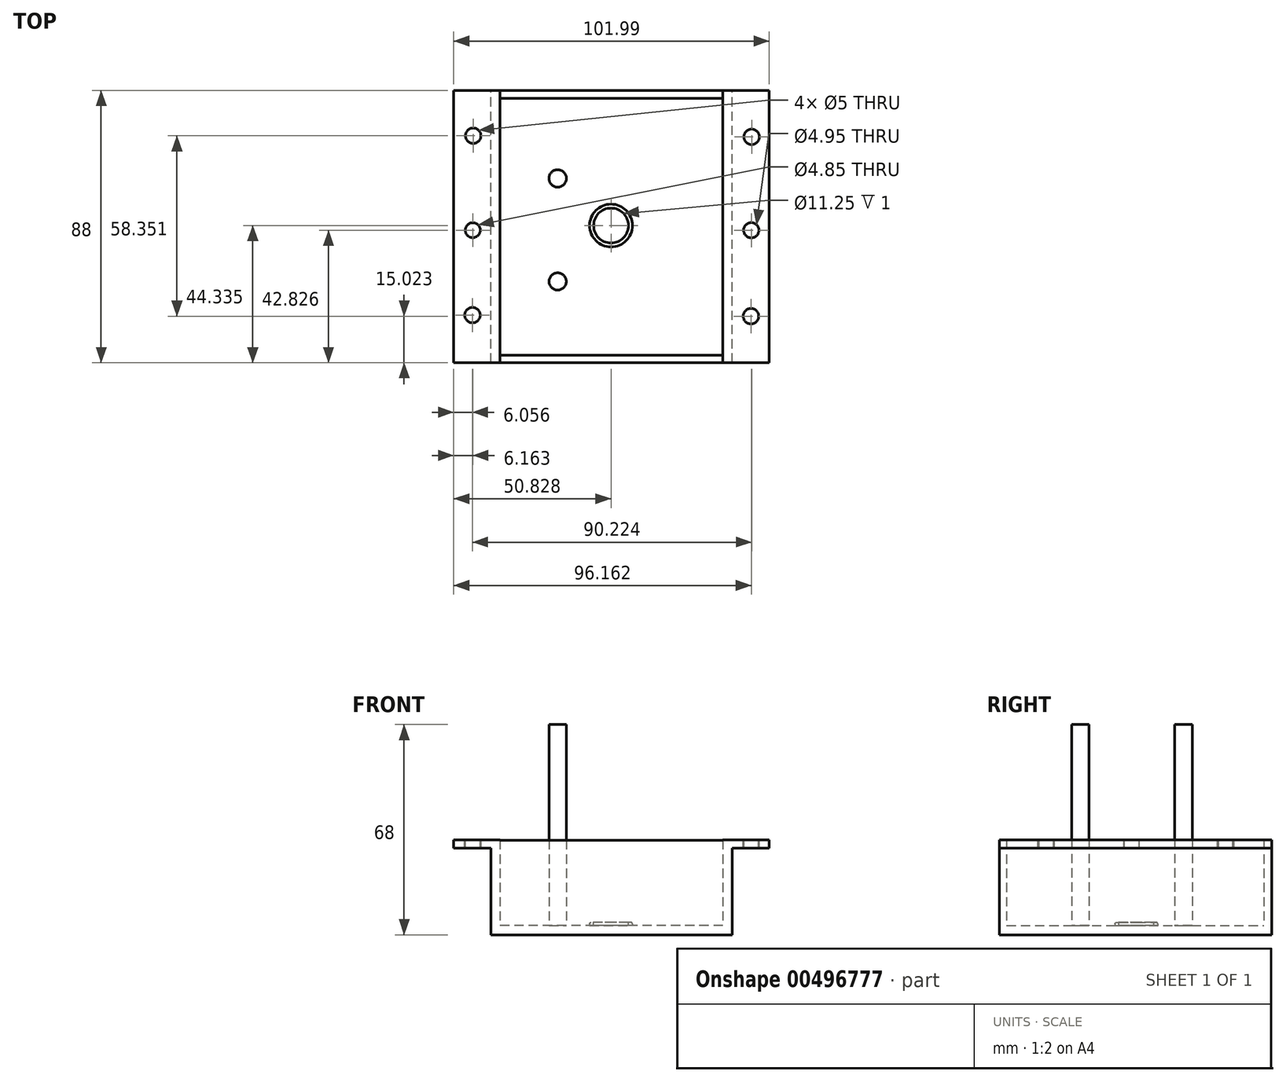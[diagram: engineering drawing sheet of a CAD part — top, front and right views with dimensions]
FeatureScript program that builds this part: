
annotation { "Feature Type Name" : "Feature", "Feature Type Description" : "" }
export const myFeature = defineFeature(function(context is Context, id is Id, definition is map)
    precondition{}
    {
        {
            var Q0;
            Q0=qCreatedBy(makeId("Front.planeOp"),FACE);
            var sketch = newSketch(context, id + "F0", { "sketchPlane" : qUnion([Q0])});
            skLineSegment(sketch, "E0", {"start": v(-2.97, -6.62) * mm, "end": v(-2.97, -9.62) * mm});
            skLineSegment(sketch, "E1", {"start": v(-2.97, -9.62) * mm, "end": v(36.03, -9.62) * mm});
            skLineSegment(sketch, "E2", {"start": v(36.03, -9.62) * mm, "end": v(36.03, 18.38) * mm});
            skLineSegment(sketch, "E3", {"start": v(36.03, 18.38) * mm, "end": v(48.02, 18.38) * mm});
            skLineSegment(sketch, "E4", {"start": v(48.02, 18.38) * mm, "end": v(48.02, 21.12) * mm});
            skLineSegment(sketch, "E5", {"start": v(48.02, 21.12) * mm, "end": v(33.02, 21.12) * mm});
            skLineSegment(sketch, "E6", {"start": v(33.02, 21.12) * mm, "end": v(33.02, -6.62) * mm});
            skLineSegment(sketch, "E7", {"start": v(33.02, -6.62) * mm, "end": v(-2.97, -6.62) * mm});
            skLineSegment(sketch, "E8.MirrorCS", {"start": v(-53.97, 18.38) * mm, "end": v(-53.97, 21.12) * mm});
            skLineSegment(sketch, "E9.MirrorCS", {"start": v(-41.97, -9.62) * mm, "end": v(-41.97, 18.38) * mm});
            skLineSegment(sketch, "E10.MirrorCS", {"start": v(-41.97, 18.38) * mm, "end": v(-53.97, 18.38) * mm});
            skLineSegment(sketch, "E11.MirrorCS", {"start": v(-53.97, 21.12) * mm, "end": v(-38.97, 21.12) * mm});
            skLineSegment(sketch, "E12.MirrorCS", {"start": v(-38.97, 21.12) * mm, "end": v(-38.97, -6.62) * mm});
            skLineSegment(sketch, "E13.MirrorCS", {"start": v(-2.97, -9.62) * mm, "end": v(-41.97, -9.62) * mm});
            skLineSegment(sketch, "E14.MirrorCS", {"start": v(-38.97, -6.62) * mm, "end": v(-2.97, -6.62) * mm});
            skPoint(sketch, "E15.MirrorCS.start.orphan", {"position": v(36.03, 18.38) * mm});
            skSolve(sketch);
        }
        {
            var Q0;
            Q0=qSketchRegion(id+"F0",true);
            extrude(context, id + "F1", {"entities" : qUnion([Q0]), "endBound" : BoundingType.SYMMETRIC, "depth" : 88 * mm});
        }
        {
            var Q0;
            Q0=makeQuery(id+"F1.opExtrude","SWEPT_FACE",FACE,{"disambiguationData":[OSD([sQuery(id+"F0.wireOp",EDGE,"E5")])]});
            var sketch = newSketch(context, id + "F2", { "sketchPlane" : qUnion([Q0])});
            skLineSegment(sketch, "E16", {"start": v(42.02, -44) * mm, "end": v(42.33, 34) * mm, "construction": true});
            skLineSegment(sketch, "E17.0.0", {"start": v(-38.97, 44) * mm, "end": v(-53.97, 44) * mm, "construction": true});
            skLineSegment(sketch, "E17.0.1", {"start": v(-53.97, 44) * mm, "end": v(-53.97, -44) * mm, "construction": true});
            skLineSegment(sketch, "E17.0.2", {"start": v(-53.97, -44) * mm, "end": v(-38.97, -44) * mm, "construction": true});
            skLineSegment(sketch, "E17.0.3", {"start": v(-38.97, -44) * mm, "end": v(-38.97, 44) * mm, "construction": true});
            skLineSegment(sketch, "E18", {"start": v(-47.67, 34) * mm, "end": v(-47.97, -44) * mm, "construction": true});
            skLineSegment(sketch, "E19", {"start": v(-53.97, -28.6) * mm, "end": v(48.02, -29) * mm, "construction": true});
            skLineSegment(sketch, "E20", {"start": v(48.02, 29) * mm, "end": v(-53.97, 29.4) * mm, "construction": true});
            skLineSegment(sketch, "E21", {"start": v(48.02, -29) * mm, "end": v(48.02, -44) * mm, "construction": true});
            skLineSegment(sketch, "E22", {"start": v(48.02, 44) * mm, "end": v(48.02, 29) * mm, "construction": true});
            skCircle(sketch, "E23", {"center": v(42.08, -28.98) * mm, "radius": 2.5 * mm});
            skCircle(sketch, "E24", {"center": v(42.31, 29.02) * mm, "radius": 2.5 * mm});
            skCircle(sketch, "E25", {"center": v(-47.69, 29.37) * mm, "radius": 2.5 * mm});
            skCircle(sketch, "E26", {"center": v(-47.91, -28.63) * mm, "radius": 2.5 * mm});
            skCircle(sketch, "E27", {"center": v(42.2, -1.17) * mm, "radius": 2.47 * mm});
            skCircle(sketch, "E28", {"center": v(-47.8, -1.17) * mm, "radius": 2.43 * mm});
            skSolve(sketch);
        }
        {
            var Q0;
            Q0=qSketchRegion(id+"F2",true);
            extrude(context, id + "F3", {"entities" : qUnion([Q0]), "operationType" : NewBodyOperationType.REMOVE, "endBound" : BoundingType.UP_TO_NEXT, "oppositeDirection" : true, "depth" : 25 * mm});
        }
        {
            var Q0;
            Q0=makeQuery(id+"F1.opExtrude","SWEPT_FACE",FACE,{"disambiguationData":[OSD([sQuery(id+"F0.wireOp",EDGE,"E7"),sQuery(id+"F0.wireOp",EDGE,"E14.MirrorCS")])]});
            var sketch = newSketch(context, id + "F4", { "sketchPlane" : qUnion([Q0])});
            skLineSegment(sketch, "E29.bottom", {"start": v(33.02, 44) * mm, "end": v(-38.97, 44) * mm});
            skLineSegment(sketch, "E29.top", {"start": v(33.02, 41.5) * mm, "end": v(-38.97, 41.5) * mm});
            skLineSegment(sketch, "E29.left", {"start": v(33.02, 44) * mm, "end": v(33.02, 41.5) * mm});
            skLineSegment(sketch, "E29.right", {"start": v(-38.97, 44) * mm, "end": v(-38.97, 41.5) * mm});
            skLineSegment(sketch, "E30.bottom", {"start": v(33.02, -44) * mm, "end": v(-38.97, -44) * mm});
            skLineSegment(sketch, "E30.top", {"start": v(33.02, -41.63) * mm, "end": v(-38.97, -41.63) * mm});
            skLineSegment(sketch, "E30.left", {"start": v(33.02, -44) * mm, "end": v(33.02, -41.63) * mm});
            skLineSegment(sketch, "E30.right", {"start": v(-38.97, -44) * mm, "end": v(-38.97, -41.63) * mm});
            skSolve(sketch);
        }
        {
            var Q0;
            Q0=qSketchRegion(id+"F4",true);
            extrude(context, id + "F5", {"entities" : qUnion([Q0]), "operationType" : NewBodyOperationType.ADD, "depth" : 27.6 * mm});
        }
        {
            var Q0;
            Q0=makeQuery(id+"F1.opExtrude","SWEPT_FACE",FACE,{"disambiguationData":[OSD([sQuery(id+"F0.wireOp",EDGE,"E7"),sQuery(id+"F0.wireOp",EDGE,"E14.MirrorCS")])]});
            var sketch = newSketch(context, id + "F6", { "sketchPlane" : qUnion([Q0])});
            skCircle(sketch, "E31", {"center": v(-3.14, 0.33) * mm, "radius": 6.92 * mm});
            skSolve(sketch);
        }
        {
            var Q0;
            Q0=qSketchRegion(id+"F6",true);
            extrude(context, id + "F7", {"entities" : qUnion([Q0]), "operationType" : NewBodyOperationType.ADD, "depth" : 1 * mm});
        }
        {
            var Q0;
            Q0=makeQuery(id+"F7.opExtrude","CAP_FACE",FACE,{"disambiguationData":[OSD([sQuery(id+"F6.wireOp",EDGE,"E31")])],"isStart":false});
            var sketch = newSketch(context, id + "F8", { "sketchPlane" : qUnion([Q0])});
            skCircle(sketch, "E32", {"center": v(-3.14, 0.33) * mm, "radius": 5.63 * mm});
            skSolve(sketch);
        }
        {
            var Q0;
            Q0=qSketchRegion(id+"F8",true);
            extrude(context, id + "F9", {"entities" : qUnion([Q0]), "operationType" : NewBodyOperationType.REMOVE, "oppositeDirection" : true, "depth" : 1 * mm});
        }
        {
            var Q0;
            Q0=makeQuery(id+"F7.opExtrude","CAP_EDGE",EDGE,{"disambiguationData":[OSD([sQuery(id+"F6.wireOp",EDGE,"E31")])],"isStart":false});
            var Q1;
            Q1=makeQuery(id+"F9.boolean.opBoolean","COPY",EDGE,{"derivedFrom":makeQuery(id+"F9.opExtrude","CAP_EDGE",EDGE,{"disambiguationData":[OSD([sQuery(id+"F8.wireOp",EDGE,"E32")])],"isStart":true})});
            fillet(context, id + "F10", {"entities" : qUnion([Q0, Q1]), "radius" : 0.5 * mm, "tangentPropagation" : true, "allowEdgeOverflow" : false});
        }
        {
            var Q0;
            Q0=makeQuery(id+"F1.opExtrude","SWEPT_FACE",FACE,{"disambiguationData":[OSD([sQuery(id+"F0.wireOp",EDGE,"E7"),sQuery(id+"F0.wireOp",EDGE,"E14.MirrorCS")])]});
            var sketch = newSketch(context, id + "F11", { "sketchPlane" : qUnion([Q0])});
            skCircle(sketch, "E33", {"center": v(-20.38, 15.57) * mm, "radius": 2.83 * mm});
            skCircle(sketch, "E34", {"center": v(-20.38, -17.74) * mm, "radius": 2.79 * mm});
            skSolve(sketch);
        }
        {
            var Q0;
            Q0=qSketchRegion(id+"F11",true);
            extrude(context, id + "F12", {"entities" : qUnion([Q0]), "operationType" : NewBodyOperationType.ADD, "depth" : 65 * mm});
        }
    });
